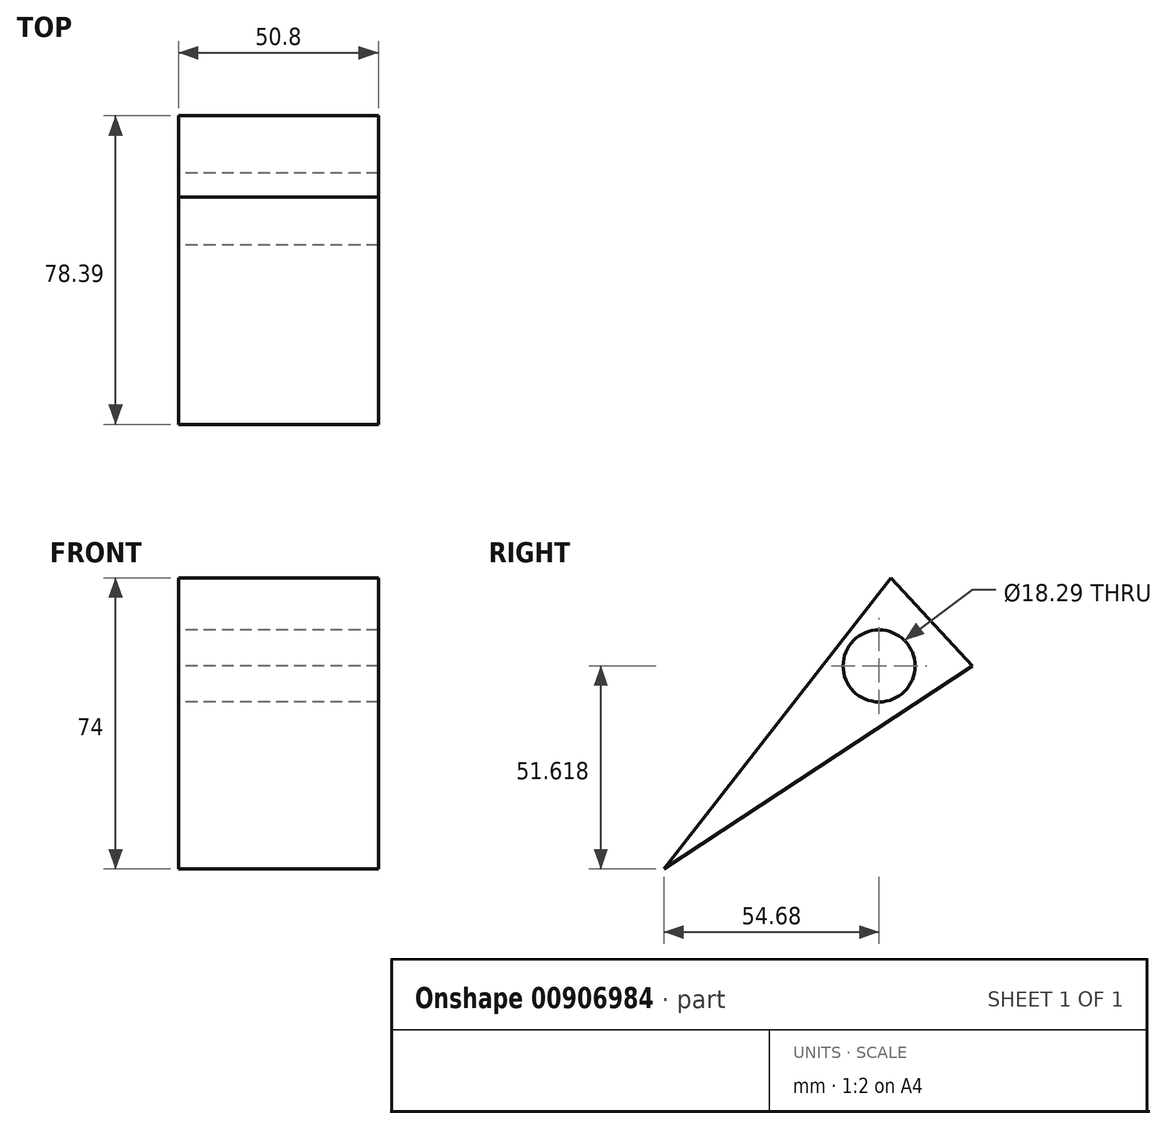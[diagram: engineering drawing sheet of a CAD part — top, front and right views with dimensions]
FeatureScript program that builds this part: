
annotation { "Feature Type Name" : "Feature", "Feature Type Description" : "" }
export const myFeature = defineFeature(function(context is Context, id is Id, definition is map)
    precondition{}
    {
        {
            var Q0;
            Q0=qCreatedBy(makeId("Right.planeOp"),FACE);
            var sketch = newSketch(context, id + "F0", { "sketchPlane" : qUnion([Q0])});
            skLineSegment(sketch, "E0", {"start": v(0, 0) * mm, "end": v(0, 0) * mm});
            skLineSegment(sketch, "E1", {"start": v(-20.69, 0) * mm, "end": v(-78.4, -74) * mm});
            skLineSegment(sketch, "E2", {"start": v(-78.4, -74) * mm, "end": v(0, -22.38) * mm});
            skLineSegment(sketch, "E3", {"start": v(0, -22.38) * mm, "end": v(74.1, -80.15) * mm});
            skLineSegment(sketch, "E4", {"start": v(74.1, -80.15) * mm, "end": v(20.69, 0) * mm});
            skLineSegment(sketch, "E5", {"start": v(20.69, 0) * mm, "end": v(0, 75.89) * mm});
            skLineSegment(sketch, "E6", {"start": v(0, 75.89) * mm, "end": v(-20.69, 0) * mm});
            skCircle(sketch, "E7", {"center": v(0, 0) * mm, "radius": 13.82 * mm});
            skCircle(sketch, "E8", {"center": v(20.69, -22.38) * mm, "radius": 9.15 * mm});
            skCircle(sketch, "E9", {"center": v(-23.7, -22.38) * mm, "radius": 9.14 * mm});
            skCircle(sketch, "E10", {"center": v(0, 28.94) * mm, "radius": 9.15 * mm});
            skLineSegment(sketch, "E11", {"start": v(-20.69, 0) * mm, "end": v(20.69, 0) * mm});
            skLineSegment(sketch, "E12", {"start": v(0, -22.38) * mm, "end": v(-20.69, 0) * mm});
            skLineSegment(sketch, "E13", {"start": v(0, -22.38) * mm, "end": v(20.69, 0) * mm});
            skSolve(sketch);
        }
        {
            var Q0;
            Q0=makeQuery(id+"F0.imprint","IMPRINT",FACE,{"disambiguationData":[TD([[makeQuery(id+"F0.imprint","IMPRINT",EDGE,{"derivedFrom":sQuery(id+"F0.wireOp",EDGE,"E1")}),1.0]])]});
            extrude(context, id + "F1", {"entities" : qUnion([Q0]), "depth" : 50.8 * mm, "offsetDistance" : 25.4 * mm});
        }
    });
